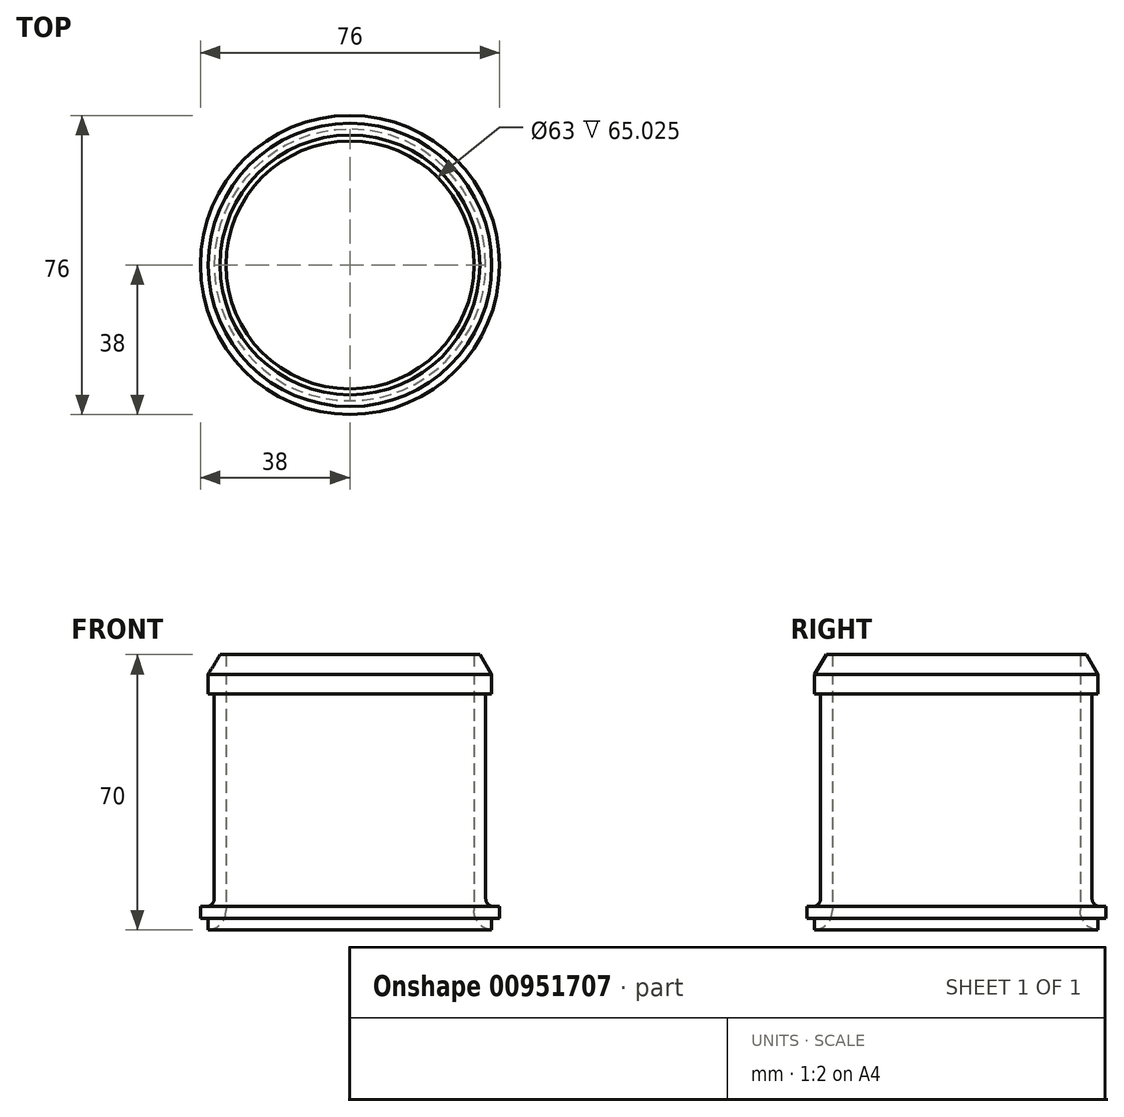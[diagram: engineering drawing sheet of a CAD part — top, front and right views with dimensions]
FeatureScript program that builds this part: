
annotation { "Feature Type Name" : "Feature", "Feature Type Description" : "" }
export const myFeature = defineFeature(function(context is Context, id is Id, definition is map)
    precondition{}
    {
        {
            var Q0;
            Q0=qCreatedBy(makeId("Front.planeOp"),FACE);
            var sketch = newSketch(context, id + "F0", { "sketchPlane" : qUnion([Q0])});
            skLineSegment(sketch, "E0", {"start": v(0, 0) * mm, "end": v(0, 70) * mm, "construction": true});
            skLineSegment(sketch, "E1", {"start": v(31.5, 70) * mm, "end": v(34.5, 70) * mm});
            skLineSegment(sketch, "E2", {"start": v(34.5, 6) * mm, "end": v(38, 6) * mm});
            skLineSegment(sketch, "E3", {"start": v(31.5, 0) * mm, "end": v(31.5, 70) * mm});
            skPoint(sketch, "E3.endSnap0", {"position": v(31.5, 70) * mm});
            skLineSegment(sketch, "E4", {"start": v(34.5, 70) * mm, "end": v(36, 70) * mm});
            skLineSegment(sketch, "E5", {"start": v(36, 70) * mm, "end": v(36, 60) * mm});
            skLineSegment(sketch, "E6", {"start": v(36, 60) * mm, "end": v(34.5, 60) * mm});
            skLineSegment(sketch, "E7", {"start": v(34.5, 60) * mm, "end": v(34.5, 6) * mm});
            skLineSegment(sketch, "E8", {"start": v(31.5, 0) * mm, "end": v(36, 0) * mm});
            skLineSegment(sketch, "E9", {"start": v(36, 0) * mm, "end": v(36, 3) * mm});
            skLineSegment(sketch, "E10", {"start": v(36, 3) * mm, "end": v(38, 3) * mm});
            skLineSegment(sketch, "E11", {"start": v(38, 3) * mm, "end": v(38, 6) * mm});
            skSolve(sketch);
        }
        {
            var Q0;
            Q0=makeQuery(id+"F0.imprint","IMPRINT",FACE,{"disambiguationData":[TD([[makeQuery(id+"F0.imprint","IMPRINT",EDGE,{"derivedFrom":sQuery(id+"F0.wireOp",EDGE,"E1")}),-1.0]])]});
            var Q1;
            Q1=sQuery(id+"F0.wireOp",EDGE,"E0");
            revolve(context, id + "F1", {"surfaceOperationType" : NewSurfaceOperationType.NEW, "entities" : qUnion([Q0]), "axis" : qUnion([Q1]), "revolveType" : RevolveType.FULL});
        }
        {
            var Q0;
            Q0=makeQuery(id+"F1.opRevolve","SWEPT_EDGE",EDGE,{"disambiguationData":[OSD([sQuery(id+"F0.wireOp",EDGE,"E4"),sQuery(id+"F0.wireOp",EDGE,"E5")])]});
            chamfer(context, id + "F2", {"entities" : qUnion([Q0]), "chamferType" : ChamferType.TWO_OFFSETS, "width1" : 5 * mm, "oppositeDirection" : false, "width2" : 3 * mm, "tangentPropagation" : true});
        }
        {
            var Q0;
            Q0=makeQuery(id+"F1.opRevolve","SWEPT_EDGE",EDGE,{"disambiguationData":[OSD([sQuery(id+"F0.wireOp",EDGE,"E2"),sQuery(id+"F0.wireOp",EDGE,"E7")])]});
            fillet(context, id + "F3", {"entities" : qUnion([Q0]), "radius" : 2 * mm, "tangentPropagation" : true, "allowEdgeOverflow" : false});
        }
        {
            var Q0;
            Q0=makeQuery(id+"F1.opRevolve","SWEPT_EDGE",EDGE,{"disambiguationData":[OSD([sQuery(id+"F0.wireOp",EDGE,"E3"),sQuery(id+"F0.wireOp",EDGE,"E8")])]});
            fillet(context, id + "F4", {"entities" : qUnion([Q0]), "radius" : 5 * mm, "tangentPropagation" : true, "allowEdgeOverflow" : false});
        }
    });
